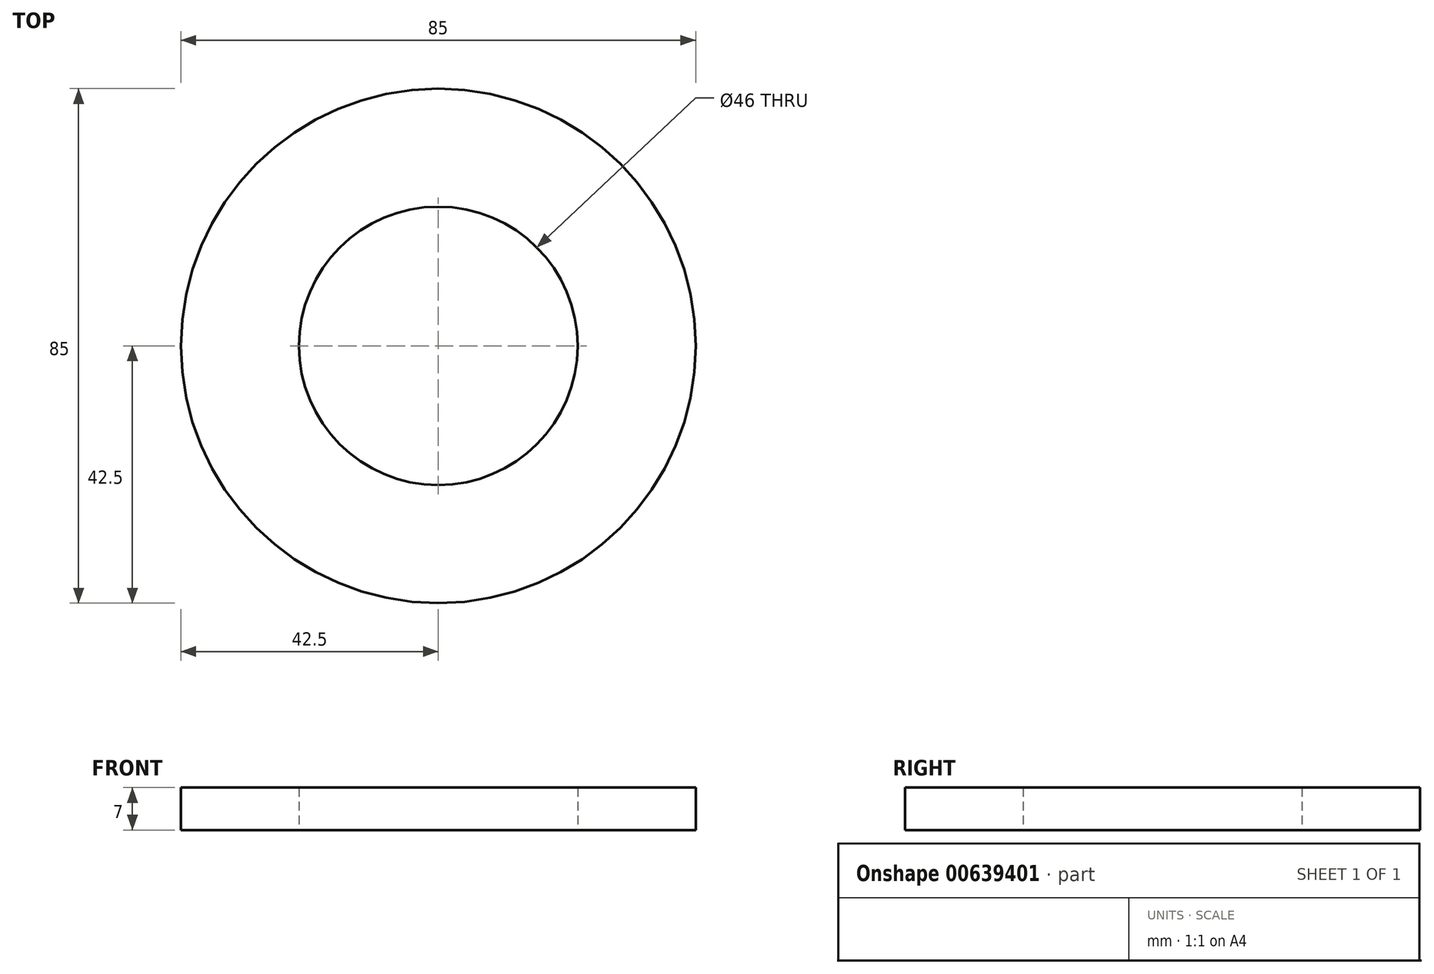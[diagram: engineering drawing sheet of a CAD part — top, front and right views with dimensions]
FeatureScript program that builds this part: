
annotation { "Feature Type Name" : "Feature", "Feature Type Description" : "" }
export const myFeature = defineFeature(function(context is Context, id is Id, definition is map)
    precondition{}
    {
        {
            var Q0;
            Q0=qCreatedBy(makeId("Top.planeOp"),FACE);
            var sketch = newSketch(context, id + "F0", { "sketchPlane" : qUnion([Q0])});
            skCircle(sketch, "E0", {"center": v(0, 0) * mm, "radius": 23 * mm});
            skCircle(sketch, "E1", {"center": v(0, 0) * mm, "radius": 42.5 * mm});
            skSolve(sketch);
        }
        {
            var Q0;
            Q0=makeQuery(id+"F0.imprint","IMPRINT",FACE,{"disambiguationData":[TD([[makeQuery(id+"F0.imprint","IMPRINT",EDGE,{"derivedFrom":sQuery(id+"F0.wireOp",EDGE,"E0")}),-1.0]])]});
            extrude(context, id + "F1", {"entities" : qUnion([Q0]), "depth" : 7 * mm, "offsetDistance" : 25 * mm});
        }
    });
